# Revit family: PRD_FrankeWS_WshBsnsWsts_RondoWasteValve_E-RNDX-SIPHON
name_source: partatom
category: Pipe Accessories
revit_build: Autodesk Revit 2018 (Build: 20190510_1515(x64)
units: mm (PartAtom-declared; Revit-internal decimal feet)

## family parameters
Always vertical = Yes
Cut with Voids When Loaded = No
OmniClass Number = 23.60.30.11.14
OmniClass Title = Pipework Fittings
Part Type = Normal
Round Connector Dimension = Use Diameter
Shared = No
Work Plane-Based = No

## types (1)
- E-RNDX-SIPHON
    AssetType = Fixed
    BIMObjectName = PRD_AR_WashBasinsWastes_RondoWasteValve_E-RNDX-SIPHON
    Category = Pr_70_55_96_97, Wash basins wastes
    Description = for RONDO washbasins, Siphon 5 / 4 ", chrome plated brass, Ø 32 mm.
    DurationUnit = year
    Features = Waste valve
    IfcExportAs = IfcWasteTerminalType
    IfcExportType = WASTETRAP
    InletConnectionSize = 0 mm  [stored 0 ft]
    InletSize = 31.75
    Manufacturer = KWC Group AG
    ManufacturerName = KWC Group AG
    ManufacturerURL = www.kwc.com
    Model = E-RNDX-SIPHON
    ModelNumber = 2000101371
    ModelReference = E-RNDX-SIPHON
    NBSDescription = Wastes for wash basins
    NBSReference = 45-35-70/372
    Name = RONDO waste valve E-RNDX-SIPHON
    NominalHeight = 0 mm  [stored 0 ft]
    NominalLength = 0 mm  [stored 0 ft]
    NominalWidth = 0 mm  [stored 0 ft]
    OutletConnectionSize = 32 mm
    OutletSize = 31.75
    ProductInformation = https://pim.kwc.com
    Shape = Cylindrical
    Size = DN 32 (5/4 inch.)
    URL = www.kwc.com
    Uniclass2015Code = Pr_70_55_96_97
    Uniclass2015Title = Wash basins wastes
    Uniclass2015Version = Products v1.5
    Version = 1
    WallOffset = 150 mm  [stored 0.492126 ft]
    WarrantyDurationUnit = year
    WasteTrapType = Other
    WasteValveMaterial = PRD_AR_ChromatedBrass

note: [stored X ft] marks values corroborated as IEEE doubles in the binary element streams (Revit-internal decimal feet)

## geometry (parser evidence)
native form markers: Sweep x3
no freeform markers — native parametric forms only
